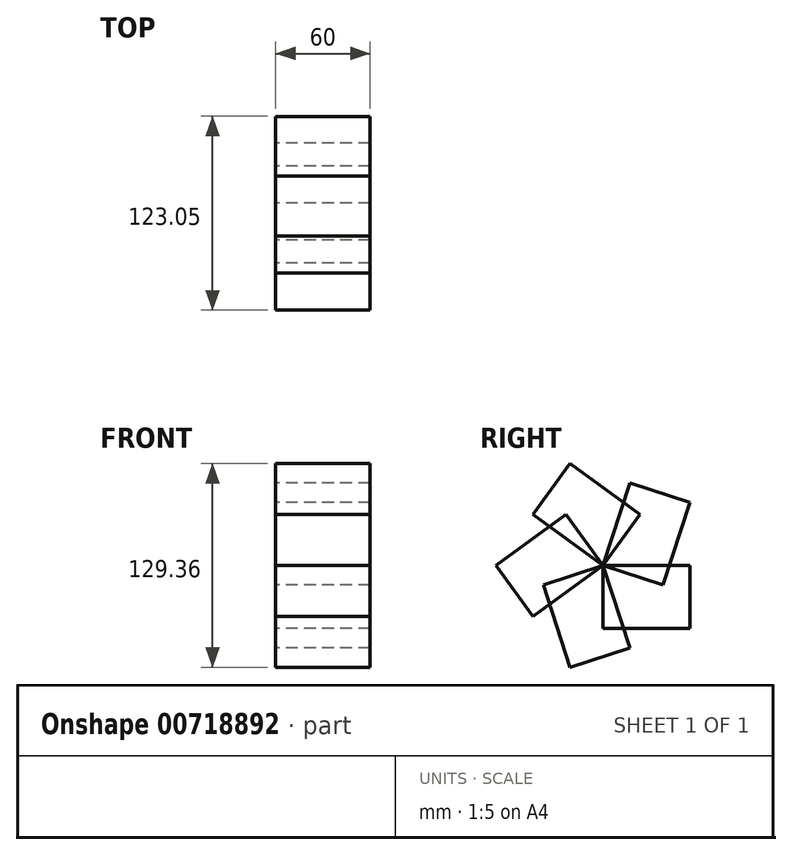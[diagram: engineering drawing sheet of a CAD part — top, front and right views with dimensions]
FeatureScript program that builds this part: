
annotation { "Feature Type Name" : "Feature", "Feature Type Description" : "" }
export const myFeature = defineFeature(function(context is Context, id is Id, definition is map)
    precondition{}
    {
        {
            var Q0;
            Q0=qCreatedBy(makeId("Top.planeOp"),FACE);
            var sketch = newSketch(context, id + "F0", { "sketchPlane" : qUnion([Q0])});
            skLineSegment(sketch, "E0.bottom", {"start": v(0, 0) * mm, "end": v(-60, 0) * mm});
            skLineSegment(sketch, "E0.top", {"start": v(0, 55) * mm, "end": v(-60, 55) * mm});
            skLineSegment(sketch, "E0.left", {"start": v(0, 0) * mm, "end": v(0, 55) * mm});
            skLineSegment(sketch, "E0.right", {"start": v(-60, 0) * mm, "end": v(-60, 55) * mm});
            skSolve(sketch);
        }
        {
            var Q0;
            Q0 = qSketchRegion(id + "F0", true);
            extrude(context, id + "F1", {"entities" : qUnion([Q0]), "depth" : 40 * mm, "offsetDistance" : 25 * mm});
        }
        {
            var Q0;
            Q0=makeQuery(id+"F1.opExtrude","SWEPT_BODY",BODY,{"disambiguationData":[OSD([sQuery(id+"F0.wireOp",EDGE,"E0.bottom"),sQuery(id+"F0.wireOp",EDGE,"E0.top"),sQuery(id+"F0.wireOp",EDGE,"E0.left"),sQuery(id+"F0.wireOp",EDGE,"E0.right")])]});
            var Q1;
            Q1=makeQuery(id+"F1.opExtrude","CAP_EDGE",EDGE,{"disambiguationData":[OSD([sQuery(id+"F0.wireOp",EDGE,"E0.bottom")])],"isStart":false});
            circularPattern(context, id + "F2", {"entities" : qUnion([Q0]), "axis" : qUnion([Q1]), "angle" : 360 * degree, "instanceCount" : 5, "equalSpace" : true});
        }
    });
